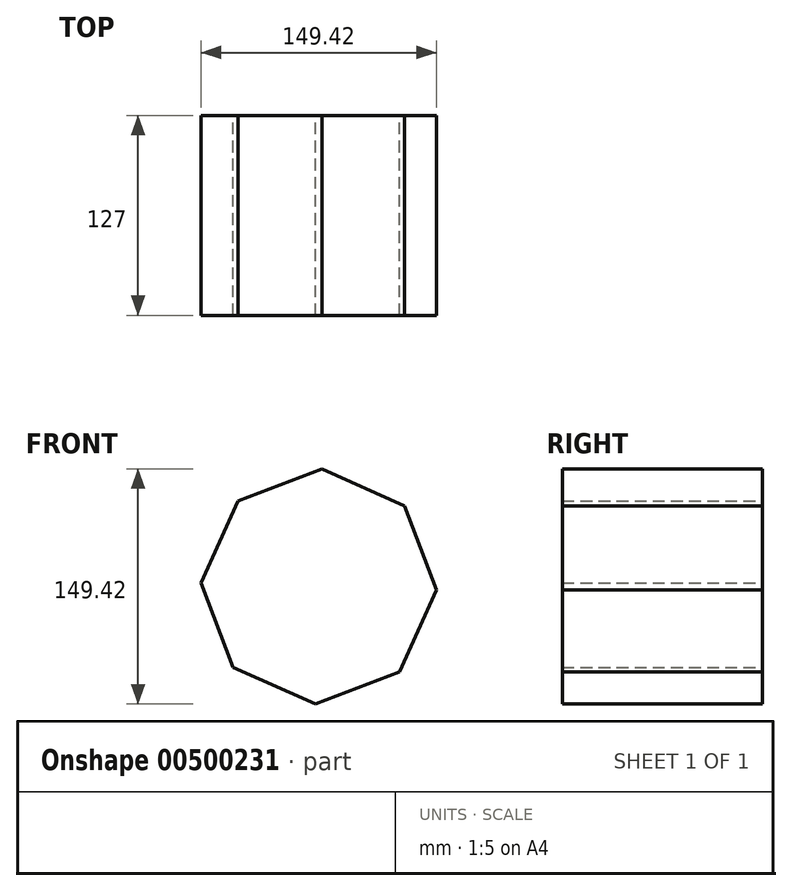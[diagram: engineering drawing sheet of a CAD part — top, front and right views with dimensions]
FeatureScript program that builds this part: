
annotation { "Feature Type Name" : "Feature", "Feature Type Description" : "" }
export const myFeature = defineFeature(function(context is Context, id is Id, definition is map)
    precondition{}
    {
        {
            var Q0;
            Q0=qCreatedBy(makeId("Front.planeOp"),FACE);
            var sketch = newSketch(context, id + "F0", { "sketchPlane" : qUnion([Q0])});
            skCircle(sketch, "E0.cCircle", {"center": v(0, 0) * mm, "radius": 74.74 * mm, "construction": true});
            skLineSegment(sketch, "E0.0", {"start": v(51.3, -54.36) * mm, "end": v(-2.16, -74.71) * mm});
            skLineSegment(sketch, "E0.1", {"start": v(-2.16, -74.71) * mm, "end": v(-54.36, -51.3) * mm});
            skLineSegment(sketch, "E0.2", {"start": v(-54.36, -51.3) * mm, "end": v(-74.71, 2.16) * mm});
            skLineSegment(sketch, "E0.3", {"start": v(-74.71, 2.16) * mm, "end": v(-51.3, 54.36) * mm});
            skLineSegment(sketch, "E0.4", {"start": v(-51.3, 54.36) * mm, "end": v(2.16, 74.71) * mm});
            skLineSegment(sketch, "E0.5", {"start": v(2.16, 74.71) * mm, "end": v(54.36, 51.3) * mm});
            skLineSegment(sketch, "E0.6", {"start": v(54.36, 51.3) * mm, "end": v(74.71, -2.16) * mm});
            skLineSegment(sketch, "E0.7", {"start": v(74.71, -2.16) * mm, "end": v(51.3, -54.36) * mm});
            skSolve(sketch);
        }
        {
            var Q0;
            Q0 = qSketchRegion(id + "F0", true);
            extrude(context, id + "F1", {"entities" : qUnion([Q0]), "depth" : 127 * mm});
        }
    });
